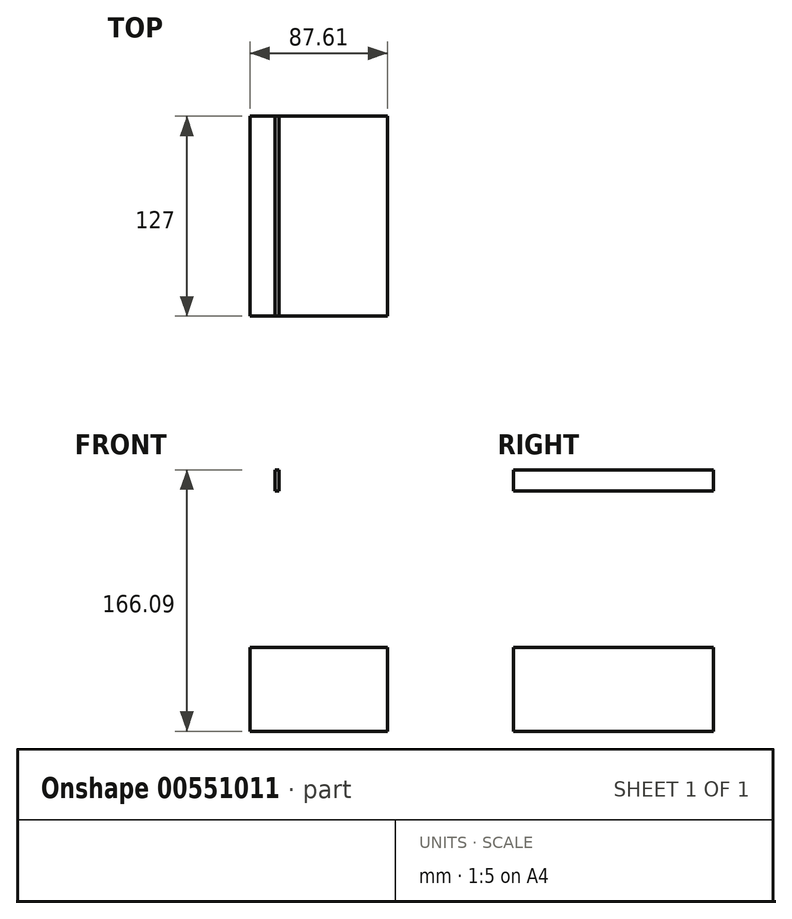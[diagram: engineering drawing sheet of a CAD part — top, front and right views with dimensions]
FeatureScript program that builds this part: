
annotation { "Feature Type Name" : "Feature", "Feature Type Description" : "" }
export const myFeature = defineFeature(function(context is Context, id is Id, definition is map)
    precondition{}
    {
        {
            var Q0;
            Q0=qCreatedBy(makeId("Front.planeOp"),FACE);
            var sketch = newSketch(context, id + "F0", { "sketchPlane" : qUnion([Q0])});
            skLineSegment(sketch, "E0.bottom", {"start": v(-87.61, 53.28) * mm, "end": v(0, 53.28) * mm});
            skLineSegment(sketch, "E0.top", {"start": v(-87.61, 0) * mm, "end": v(0, 0) * mm});
            skLineSegment(sketch, "E0.left", {"start": v(-87.61, 53.28) * mm, "end": v(-87.61, 0) * mm});
            skLineSegment(sketch, "E0.right", {"start": v(0, 53.28) * mm, "end": v(0, 0) * mm});
            skLineSegment(sketch, "E1.bottom", {"start": v(-71.64, 152.46) * mm, "end": v(-69.06, 152.46) * mm});
            skLineSegment(sketch, "E1.top", {"start": v(-71.64, 166.1) * mm, "end": v(-69.06, 166.1) * mm});
            skLineSegment(sketch, "E1.left", {"start": v(-71.64, 152.46) * mm, "end": v(-71.64, 166.1) * mm});
            skLineSegment(sketch, "E1.right", {"start": v(-69.06, 152.46) * mm, "end": v(-69.06, 166.1) * mm});
            skSolve(sketch);
        }
        {
            var Q0;
            Q0 = qSketchRegion(id + "F0", true);
            var Q1;
            Q1=makeQuery(id+"F0.imprint","IMPRINT",FACE,{"disambiguationData":[TD([[makeQuery(id+"F0.imprint","IMPRINT",EDGE,{"derivedFrom":sQuery(id+"F0.wireOp",EDGE,"E0.bottom")}),-1.0]])]});
            extrude(context, id + "F1", {"entities" : qUnion([Q0, Q1]), "depth" : 127 * mm, "offsetDistance" : 25.4 * mm});
        }
    });
